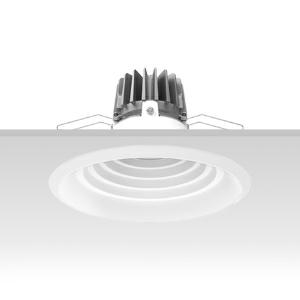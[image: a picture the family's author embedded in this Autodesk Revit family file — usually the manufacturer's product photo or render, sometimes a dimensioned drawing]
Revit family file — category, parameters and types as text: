
# Revit family: 3f_filippi_-_3f_reno_bianco_ampio_3f_filippi_-_30671_-_3f_reno_200_wh_2000-840_dali_wide
name_source: partatom
category: Lighting Fixtures
units: mm (PartAtom-declared; Revit-internal decimal feet)

## family parameters
Cut with Voids When Loaded = No
Host = Face
Light Source = No
Part Type = Normal
Room Calculation Point = No
Round Connector Dimension = Use Diameter
Shared = No

## types (1)
- 3F Filippi - 3F Reno Bianco Ampio (1 x LED, 1963 lm, 20 W, 4000 K)
    Apparent Load = 20 VA
    Approval mark = CE
    CIE Flux Codes = 80 97 100 100 100
    Color Rendering = 80
    Color Temperature = 4000 K
    Control Gear = Electronic transformer
    Default Elevation = 1800 mm
    Description = ILLUMINOTECHNICAL
Luminous efficiency 100% (DLOR 100%, ULOR 0%).
Initial luminous flux of the luminaire 1963 lm.
Direct symmetric wide distribution.
Installation Interdistance Transv.D = 1.56 x hu - Long.D = 1.56 x hu.
Average luminance <3000 cd/m² for radial angles >65°.
Tabular UGR (CIE 117 - 4H-8H; S=0.25H; 70/50/20): RUG 19.3 - 19.4.
Beam angle: 85° - 84°.
Luminous efficacy 98 lm/W.
Lifetime (L90/B10): 30000 h. (tq+25°C)
Lifetime (L85/B10): 50000 h. (tq+25°C)
Lifetime (L70/B10): 80000 h. (tq+25°C)
Sudden decreased luminous flux after 50000 hours: 0% (C0).
Photobiological safety in compliance with IEC/TR 62778: RG0 risk exempt, (IEC 62471).
In compliance with IEC/EN 62722-2-1 - IEC/EN 62717 standards.

SOURCE
Compact LED module 2000/840.
Energy efficiency class (UE 2019/2020 - UE 2019/2015): D.
CIE 13.3 Colour rendering index: CRI >80 (R9 <50%).
IES TM-30 Fidelity Index: Rf = 84 Rg = 95.
CCT nominal colour temperature 4000 K.
Colour initial tolerance (MacAdam): SDCM 3.
Zhaga Book 3 compliant.

MECHANICAL
Passive heat dissipator in die-casting aluminium, oversized, for optimum thermal management of the LED module.
Parabolic element with graduated/concentric rings in white polycarbonate.
Transparent external lens with glossy and satin differentiated surfaces, with a cooling and anti-insect system in methacrylate (PMMA).
Fastening spring clips in stainless steel.
Dimensions: diameter 216 mm, height 142 mm. Weight 0.9 kg.
IP44 protection degree for exposed part, IP20 for recessed part.
Mechanical strength to impacts IK04 (0.5 joule).
Glow-wire test resistance 650°C.

ELECTRICAL
Wiring on a separate unit.
Halogen Free DALI-2 DATI (Parts 251, 252, 253), PUSH-DIM, electronic wiring 230V-50/60Hz, power factor 0.90 at full load, THD <25%, constant output current, SELV, class II, 1 driver, 1 DALI addresse.
Power of the luminaire 20 W.
ENEC - CE.
SAFE FLICKER: PstLM=<1 and SVM=<0.4 (IEC TR 61547-1 and IEC TR 63158), to ensure a more comfortable and safe light.
Luminaire compliant with EN 60598-2-22 for power supply from a centralised emergency system CPSS (Central Power Supply System), not incorporated in the luminaire - high risk areas excluded. The default power and flux are 100% in AC and 100% in DC.
Ambient temperature from 0°C to +25°C.
Temperature class T6 max 85°C.
Relative humidity UR: <85%.

INSTALLATION
Pull-up recessed fitting.
False ceiling carving: 200 mm.
All accessories dedicated to this product are available on the Catalog and on our website www.3F-Filippi.com.

APPLICATIONS
Environments: architectural, commercial, exhibition areas, transit areas, corridors, shops, display windows, service areas.
In false ceilings with narrow voids.

LIGHT MANAGEMENT
Recommended minimum setting: 10%.
The luminaire, equipped with (DALI-2 DATI) driver, can be controlled manually with 3F Easy Dim technology or automatically/manually with wired or wireless DALI/D2D control systems.
The D2D driver guarantees interoperability with other devices with the same certification by making the following information available:
Device Data (Part 251), Energy Report (Part 252), Diagnosis & Maintenance (Part 253).
In electrical systems without a regulation system (manual or automatic) and DALI bus, a suitable jumper must be made on the DA-DA terminals of the appliance.

WARNING
Luminaire designed for disposal/recycling at end-of-life.
Replaceable (LED only) light source by a professional. Replaceable control gear by a professional.
    Height = 0 mm  [stored 0 ft]
    Lamp = 1 x LED
    Lamp Light Flux = 1963 lm
    Lamp Power = 20 W
    Lamp count = 1
    Length = 216 mm
    Lifetime = 50000 h
    Luminous efficacy = 98 lm/W
    Manufacturer = 3F Filippi
    ModVariant = No
    Model = 3F Filippi - 30671 - 3F Reno 200 WH 2000-840 DALI WIDE
    Mounting Place = Ceiling
    Mounting Type = Recessed
    Number of Poles = 1
    OnlyDefault = Yes
    Power Factor = 1
    Product Name = 3F Filippi - 3F Reno Bianco Ampio
    Product group = recessed luminaire
    ProductGroupID = 4
    Protection Class = Protection class II
    Protection Degree = IP 20
    RLX_Detail_Level = 1
    RLX_Emergency_Light_Flux = 0 lm
    RLX_Emergency_Type = 0
    RLX_Emergency_Type_DB = No
    RlxData = <blob elided: 90301 chars, md5=3d72a1b7>
    Socket = socket
    Standby Power = 0 W
    System Light Flux = 1963 lm
    System Power = 20 W
    Type Comments = Product without accessories
    Type Image = 3ffilippi_3f_reno_200_wh_2000.jpg
    URL = http://relux.com
    VarID = ---
    Voltage = 0 V
    Weight = 0.00 kg
    Width = 0 mm  [stored 0 ft]

note: [stored X ft] marks values corroborated as IEEE doubles in the binary element streams (Revit-internal decimal feet)

## geometry (parser evidence)
native form markers: Blend x4, Sweep x10
no freeform markers — native parametric forms only
